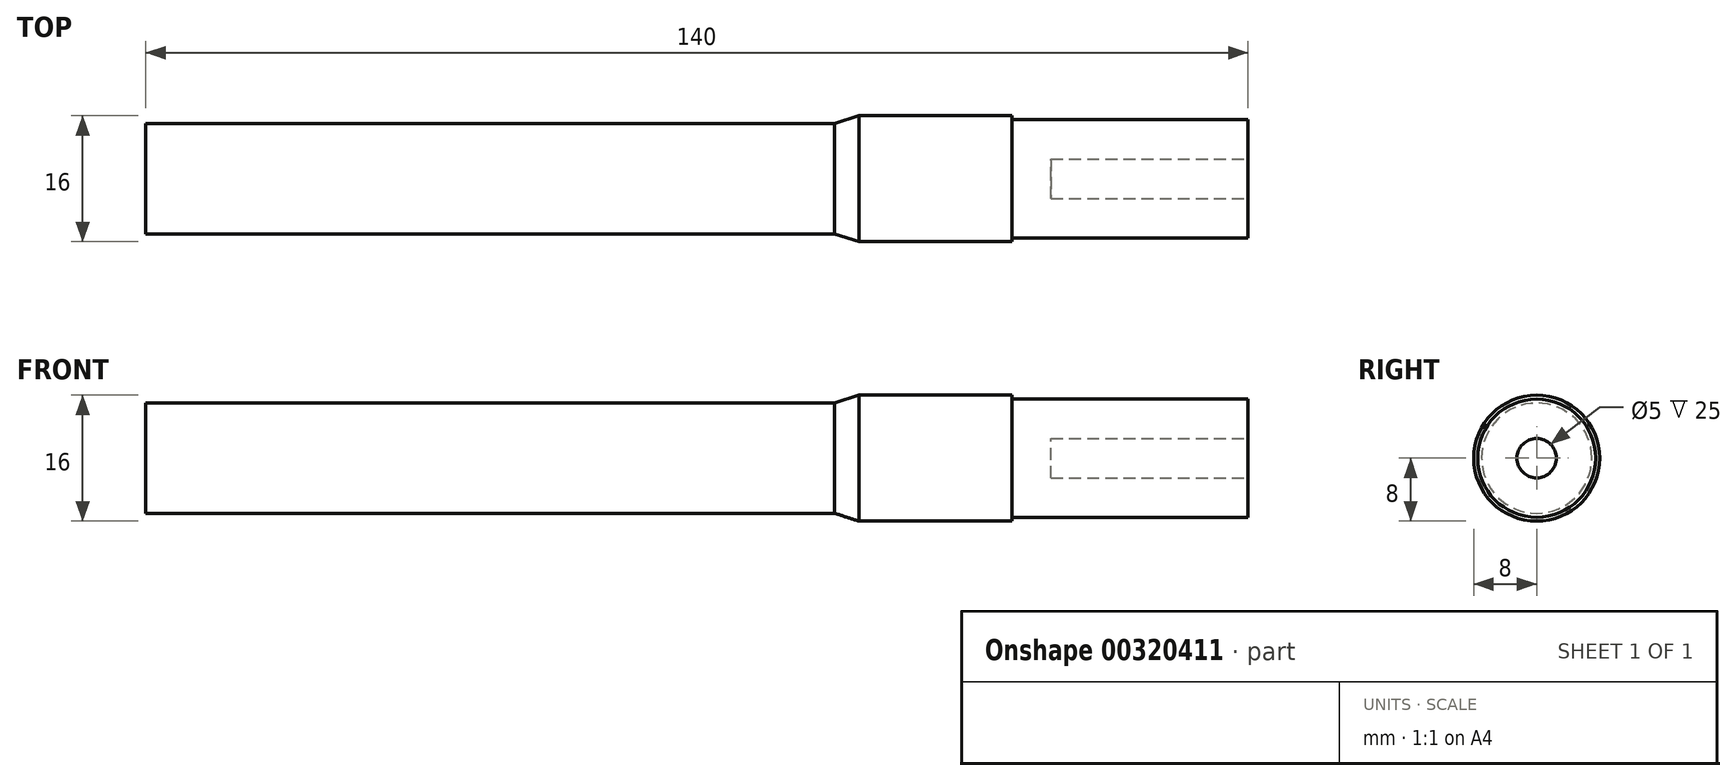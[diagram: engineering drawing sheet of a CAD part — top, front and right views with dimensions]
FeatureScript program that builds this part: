
annotation { "Feature Type Name" : "Feature", "Feature Type Description" : "" }
export const myFeature = defineFeature(function(context is Context, id is Id, definition is map)
    precondition{}
    {
        {
            var Q0;
            Q0=qCreatedBy(makeId("Front.planeOp"),FACE);
            var sketch = newSketch(context, id + "F0", { "sketchPlane" : qUnion([Q0])});
            skLineSegment(sketch, "E0", {"start": v(-11.78, 0) * mm, "end": v(-151.78, 0) * mm});
            skLineSegment(sketch, "E1", {"start": v(-151.78, 0) * mm, "end": v(-151.78, 7) * mm});
            skLineSegment(sketch, "E2", {"start": v(-151.78, 7) * mm, "end": v(-98.28, 7) * mm});
            skLineSegment(sketch, "E3", {"start": v(-98.28, 7) * mm, "end": v(-64.28, 7) * mm});
            skLineSegment(sketch, "E4", {"start": v(-64.28, 7) * mm, "end": v(-61.2, 8) * mm});
            skLineSegment(sketch, "E5", {"start": v(-98.28, 7) * mm, "end": v(-91.78, 7) * mm});
            skLineSegment(sketch, "E6", {"start": v(-151.78, 5.5) * mm, "end": v(-98.78, 5.5) * mm});
            skLineSegment(sketch, "E7", {"start": v(-11.78, 0) * mm, "end": v(-11.78, 7.5) * mm});
            skLineSegment(sketch, "E8", {"start": v(-11.78, 7.5) * mm, "end": v(-41.78, 7.5) * mm});
            skLineSegment(sketch, "E9", {"start": v(-41.78, 7.5) * mm, "end": v(-41.78, 8) * mm});
            skLineSegment(sketch, "E10", {"start": v(-61.2, 8) * mm, "end": v(-41.78, 8) * mm});
            skSolve(sketch);
        }
        {
            var Q0;
            {var subQ0=sQuery(id+"F0.wireOp",EDGE,"E0");Q0=makeQuery(id+"F0.imprint","IMPRINT",FACE,{"disambiguationData":[TD([[makeQuery(id+"F0.imprint","IMPRINT",EDGE,{"derivedFrom":subQ0}),-1.0]])]});}
            var Q1;
            Q1=sQuery(id+"F0.wireOp",EDGE,"E0");
            revolve(context, id + "F1", {"entities" : qUnion([Q0]), "axis" : qUnion([Q1]), "revolveType" : RevolveType.FULL});
        }
        {
            var Q0;
            Q0=makeQuery(id+"F1.opRevolve","SWEPT_FACE",FACE,{"disambiguationData":[OSD([sQuery(id+"F0.wireOp",EDGE,"E7")])]});
            var sketch = newSketch(context, id + "F2", { "sketchPlane" : qUnion([Q0])});
            skSolve(sketch);
        }
        {
            var Q0;
            Q0=makeQuery(id+"F2.imprint","IMPRINT",FACE,{"disambiguationData":[TD([[makeQuery(id+"F2.imprint","IMPRINT",EDGE,{"derivedFrom":makeQuery(id+"F1.opRevolve","SWEPT_EDGE",EDGE,{"disambiguationData":[OSD([sQuery(id+"F0.wireOp",EDGE,"E7"),sQuery(id+"F0.wireOp",EDGE,"E8")])]})}),1.0]])]});
            var sketch = newSketch(context, id + "F3", { "sketchPlane" : qUnion([Q0])});
            skCircle(sketch, "E11", {"center": v(0, 0) * mm, "radius": 3 * mm});
            skCircle(sketch, "E12", {"center": v(0, 0) * mm, "radius": 2.5 * mm});
            skSolve(sketch);
        }
        {
            var Q0;
            Q0=makeQuery(id+"F3.imprint","IMPRINT",FACE,{"disambiguationData":[TD([[makeQuery(id+"F3.imprint","IMPRINT",EDGE,{"derivedFrom":sQuery(id+"F3.wireOp",EDGE,"E12")}),1.0]])]});
            var Q1;
            Q1=sQuery(id+"F3.wireOp",EDGE,"E12");
            extrude(context, id + "F4", {"entities" : qUnion([Q0]), "operationType" : NewBodyOperationType.REMOVE, "surfaceEntities" : qUnion([Q1]), "oppositeDirection" : true, "depth" : 25 * mm});
        }
    });
